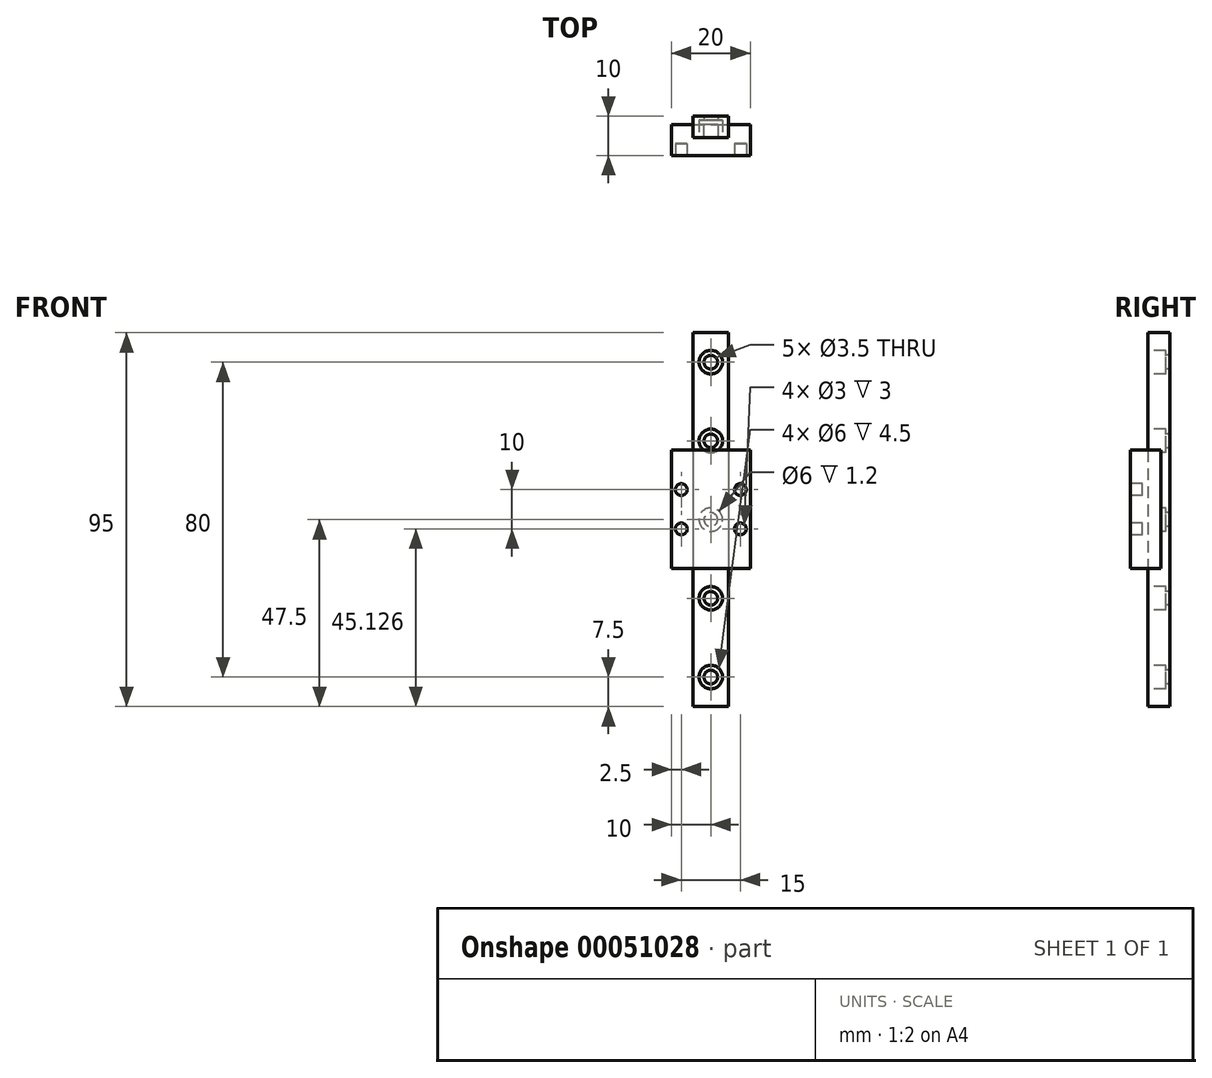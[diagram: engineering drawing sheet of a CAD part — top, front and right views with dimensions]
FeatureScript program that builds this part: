
annotation { "Feature Type Name" : "Feature", "Feature Type Description" : "" }
export const myFeature = defineFeature(function(context is Context, id is Id, definition is map)
    precondition{}
    {
        {
            var Q0;
            Q0=qCreatedBy(makeId("Front.planeOp"),FACE);
            var sketch = newSketch(context, id + "F0", { "sketchPlane" : qUnion([Q0])});
            skLineSegment(sketch, "E0.bottom", {"start": v(-4.5, 47.5) * mm, "end": v(4.5, 47.5) * mm});
            skLineSegment(sketch, "E0.top", {"start": v(-4.5, -47.5) * mm, "end": v(4.5, -47.5) * mm});
            skLineSegment(sketch, "E0.left", {"start": v(-4.5, 47.5) * mm, "end": v(-4.5, -47.5) * mm});
            skLineSegment(sketch, "E0.right", {"start": v(4.5, 47.5) * mm, "end": v(4.5, -47.5) * mm});
            skLineSegment(sketch, "E1", {"start": v(0, 20.52) * mm, "end": v(0, -25.9) * mm, "construction": true});
            skLineSegment(sketch, "E2", {"start": v(-19.4, 0) * mm, "end": v(19.83, 0) * mm, "construction": true});
            skSolve(sketch);
        }
        {
            var Q0;
            Q0 = qSketchRegion(id + "F0", true);
            extrude(context, id + "F1", {"entities" : qUnion([Q0]), "depth" : 5.5 * mm});
        }
        {
            var Q0;
            Q0=makeQuery(id+"F1.opExtrude","CAP_FACE",FACE,{"disambiguationData":[OSD([sQuery(id+"F0.wireOp",EDGE,"E0.bottom"),sQuery(id+"F0.wireOp",EDGE,"E0.top"),sQuery(id+"F0.wireOp",EDGE,"E0.left"),sQuery(id+"F0.wireOp",EDGE,"E0.right")])],"isStart":false});
            var sketch = newSketch(context, id + "F2", { "sketchPlane" : qUnion([Q0])});
            skCircle(sketch, "E3", {"center": v(0, 40) * mm, "radius": 1.75 * mm});
            skCircle(sketch, "E4.1.0.0", {"center": v(0, 20) * mm, "radius": 1.75 * mm});
            skCircle(sketch, "E4.2.0.0", {"center": v(0, 0) * mm, "radius": 1.75 * mm});
            skLineSegment(sketch, "E4.direction1", {"start": v(0, 40) * mm, "end": v(0, 20) * mm, "construction": true});
            skCircle(sketch, "E5.0.3.0", {"center": v(0, -20) * mm, "radius": 1.75 * mm});
            skCircle(sketch, "E5.0.4.0", {"center": v(0, -40) * mm, "radius": 1.75 * mm});
            skLineSegment(sketch, "E6", {"start": v(0, 56.3) * mm, "end": v(0, -59.9) * mm, "construction": true});
            skCircle(sketch, "E7", {"center": v(0, 40) * mm, "radius": 3 * mm});
            skCircle(sketch, "E8.1.0.0", {"center": v(0, 20) * mm, "radius": 3 * mm});
            skCircle(sketch, "E8.2.0.0", {"center": v(0, 0) * mm, "radius": 3 * mm});
            skCircle(sketch, "E9.0.3.0", {"center": v(0, -20) * mm, "radius": 3 * mm});
            skCircle(sketch, "E9.0.4.0", {"center": v(0, -40) * mm, "radius": 3 * mm});
            skSolve(sketch);
        }
        {
            var Q0;
            Q0=makeQuery(id+"F2.imprint","IMPRINT",FACE,{"disambiguationData":[TD([[makeQuery(id+"F2.imprint","IMPRINT",EDGE,{"derivedFrom":sQuery(id+"F2.wireOp",EDGE,"E4.1.0.0")}),1.0]])]});
            var Q1;
            Q1=makeQuery(id+"F2.imprint","IMPRINT",FACE,{"disambiguationData":[TD([[makeQuery(id+"F2.imprint","IMPRINT",EDGE,{"derivedFrom":sQuery(id+"F2.wireOp",EDGE,"E3")}),1.0]])]});
            var Q2;
            Q2=makeQuery(id+"F2.imprint","IMPRINT",FACE,{"disambiguationData":[TD([[makeQuery(id+"F2.imprint","IMPRINT",EDGE,{"derivedFrom":sQuery(id+"F2.wireOp",EDGE,"E4.2.0.0")}),1.0]])]});
            var Q3;
            Q3=makeQuery(id+"F2.imprint","IMPRINT",FACE,{"disambiguationData":[TD([[makeQuery(id+"F2.imprint","IMPRINT",EDGE,{"derivedFrom":sQuery(id+"F2.wireOp",EDGE,"E5.0.3.0")}),1.0]])]});
            var Q4;
            Q4=makeQuery(id+"F2.imprint","IMPRINT",FACE,{"disambiguationData":[TD([[makeQuery(id+"F2.imprint","IMPRINT",EDGE,{"derivedFrom":sQuery(id+"F2.wireOp",EDGE,"E5.0.4.0")}),1.0]])]});
            extrude(context, id + "F3", {"entities" : qUnion([Q0, Q1, Q2, Q3, Q4]), "operationType" : NewBodyOperationType.REMOVE, "endBound" : BoundingType.THROUGH_ALL, "oppositeDirection" : true, "depth" : 25 * mm});
        }
        {
            var Q0;
            Q0 = qSketchRegion(id + "F2", true);
            extrude(context, id + "F4", {"entities" : qUnion([Q0]), "operationType" : NewBodyOperationType.REMOVE, "oppositeDirection" : true, "depth" : 4.5 * mm});
        }
        {
            var Q0;
            Q0=qCreatedBy(makeId("Front.planeOp"),FACE);
            cPlane(context, id + "F5", {"entities" : qUnion([Q0]), "cplaneType" : CPlaneType.OFFSET, "offset" : 2.2 * mm, "width" : 150 * mm, "height" : 150 * mm});
        }
        {
            var Q0;
            Q0=qCreatedBy(id+"F5.planeOp",FACE);
            var sketch = newSketch(context, id + "F6", { "sketchPlane" : qUnion([Q0])});
            skLineSegment(sketch, "E10.bottom", {"start": v(-10, 17.63) * mm, "end": v(10, 17.63) * mm});
            skLineSegment(sketch, "E10.top", {"start": v(-10, -12.37) * mm, "end": v(10, -12.37) * mm});
            skLineSegment(sketch, "E10.left", {"start": v(-10, 17.63) * mm, "end": v(-10, -12.37) * mm});
            skLineSegment(sketch, "E10.right", {"start": v(10, 17.63) * mm, "end": v(10, -12.37) * mm});
            skSolve(sketch);
        }
        {
            var Q0;
            Q0=makeQuery(id+"F6.imprint","IMPRINT",FACE,{"disambiguationData":[TD([[makeQuery(id+"F6.imprint","IMPRINT",EDGE,{"derivedFrom":sQuery(id+"F6.wireOp",EDGE,"E10.bottom")}),-1.0]])]});
            var Q1;
            Q1=sQuery(id+"F6.wireOp",EDGE,"E10.bottom");
            extrude(context, id + "F7", {"entities" : qUnion([Q0]), "surfaceEntities" : qUnion([Q1]), "depth" : 7.8 * mm});
        }
        {
            var Q0;
            Q0=makeQuery(id+"F7.opExtrude","CAP_FACE",FACE,{"disambiguationData":[OSD([sQuery(id+"F6.wireOp",EDGE,"E10.bottom"),sQuery(id+"F6.wireOp",EDGE,"E10.top"),sQuery(id+"F6.wireOp",EDGE,"E10.left"),sQuery(id+"F6.wireOp",EDGE,"E10.right")])],"isStart":true});
            var sketch = newSketch(context, id + "F8", { "sketchPlane" : qUnion([Q0])});
            skLineSegment(sketch, "E11.bottom", {"start": v(-4.5, 17.63) * mm, "end": v(4.5, 17.63) * mm});
            skLineSegment(sketch, "E11.top", {"start": v(-4.5, -12.37) * mm, "end": v(4.5, -12.37) * mm});
            skLineSegment(sketch, "E11.left", {"start": v(-4.5, 17.63) * mm, "end": v(-4.5, -12.37) * mm});
            skLineSegment(sketch, "E11.right", {"start": v(4.5, 17.63) * mm, "end": v(4.5, -12.37) * mm});
            skSolve(sketch);
        }
        {
            var Q0;
            Q0 = qSketchRegion(id + "F8", true);
            var Q1;
            Q1=makeQuery(id+"F1.opExtrude","CAP_FACE",FACE,{"disambiguationData":[OSD([sQuery(id+"F0.wireOp",EDGE,"E0.bottom"),sQuery(id+"F0.wireOp",EDGE,"E0.top"),sQuery(id+"F0.wireOp",EDGE,"E0.left"),sQuery(id+"F0.wireOp",EDGE,"E0.right")])],"isStart":false});
            extrude(context, id + "F9", {"entities" : qUnion([Q0]), "operationType" : NewBodyOperationType.REMOVE, "endBound" : BoundingType.UP_TO_SURFACE, "oppositeDirection" : true, "endBoundEntityFace" : qUnion([Q1]), "depth" : 25 * mm});
        }
        {
            var Q0;
            Q0=makeQuery(id+"F7.opExtrude","CAP_FACE",FACE,{"disambiguationData":[OSD([sQuery(id+"F6.wireOp",EDGE,"E10.bottom"),sQuery(id+"F6.wireOp",EDGE,"E10.top"),sQuery(id+"F6.wireOp",EDGE,"E10.left"),sQuery(id+"F6.wireOp",EDGE,"E10.right")])],"isStart":false});
            var sketch = newSketch(context, id + "F10", { "sketchPlane" : qUnion([Q0])});
            skLineSegment(sketch, "E12", {"start": v(0, 32.73) * mm, "end": v(0, -15.6) * mm, "construction": true});
            skLineSegment(sketch, "E13", {"start": v(-21.44, 2.63) * mm, "end": v(23.02, 2.63) * mm, "construction": true});
            skCircle(sketch, "E14", {"center": v(-7.5, 7.63) * mm, "radius": 1.5 * mm});
            skCircle(sketch, "E15.MirrorC", {"center": v(7.5, 7.63) * mm, "radius": 1.5 * mm});
            skCircle(sketch, "E16.MirrorC", {"center": v(7.5, -2.37) * mm, "radius": 1.5 * mm});
            skCircle(sketch, "E17.MirrorC", {"center": v(-7.5, -2.37) * mm, "radius": 1.5 * mm});
            skSolve(sketch);
        }
        {
            var Q0;
            Q0 = qSketchRegion(id + "F10", true);
            extrude(context, id + "F11", {"entities" : qUnion([Q0]), "operationType" : NewBodyOperationType.REMOVE, "oppositeDirection" : true, "depth" : 3 * mm});
        }
    });
